# Revit family: LED-PL-CSVT
name_source: partatom
category: Осветительные приборы
units: mm (PartAtom-declared; Revit-internal decimal feet)

## family parameters
Всегда вертикально = Нет
Источник света = Да
На основе рабочей плоскости = Нет
Общий = Нет
При загрузке вырезать с полостями = Нет
Размер круглого соединителя = Использовать диаметр
Тип детали = Нормальный
Точка расчета площади = Да

## types (9) — shared parameters
ADSK_Единица измерения = шт.
ADSK_Завод-изготовитель = ЗАО «Центрстройсвет»
ADSK_Классификация нагрузок = Прочее
ADSK_Количество фаз = 1
ADSK_Количество фаз числовое = 1
ADSK_Коэффициент мощности = 0.92
ADSK_Напряжение = 230 В
ADSK_Ток = 0 А
URL = http://csvt.ru
Видимая форма излучения при визуализации = Да
Высота = 10 мм
Изготовитель = ЗАО «Центрстройсвет»
Материал светильника = RAL 9001
Материал стекла = RAL светящийся
Светофильтр = 16777215
Смещение цветовой температуры при затухании лампы = <Нет>
Угол наклона = 90.00°

## per-type parameters (varying)
| type | ADSK_Код изделия | ADSK_Масса | ADSK_Наименование | ADSK_Номинальная мощность | ADSK_Обозначение | ADSK_Полная мощность | L | L1 | Длина | Излучение по длине прямоугольника | Излучение по ширине прямоугольника | Файл фотометрической сетки | Ширина |
| LED PL-CSVT-36 595x595х10 (KROKUS) (IP54/IP20, 4000K, белый) | ЦБ000007456 | 3.2 | Ультратонкая светодиодная панель LED PL-CSVT-36 595x595х10 (KROKUS) (IP54/IP20, 4000K, белый) | 36 Вт | LED PL-CSVT-36 595x595х10 (KROKUS) (IP54/IP20, 4000K, белый) | 39 В·А | 298 мм | 298 мм | 595 мм | 555 мм | 555 мм | Светильник LED-PL-CSVT-36-(595х595).IES | 595 мм |
| LED PL-CSVT-36 595x595 х10 (KROKUS) (IP54/IP20, 4000K, белый) c БАП на 1 час | ЦБ000007518 | 3.2 | Ультратонкая светодиодная панель LED PL-CSVT-36 595x595 х10 (KROKUS) (IP54/IP20, 4000K, белый) c БАП на 1 час | 36 Вт | LED PL-CSVT-36 595x595 х10 (KROKUS) (IP54/IP20, 4000K, белый) | 39 В·А | 298 мм | 298 мм | 595 мм | 555 мм | 555 мм | Светильник LED-PL-CSVT-36-(595х595).IES | 595 мм |
| LED PL-CSVT-36 595x595 х10 (KROKUS) (IP54/IP20, 4000K, белый) c БАП на 3 часа | ЦБ000007519 | 3.2 | Ультратонкая светодиодная панель LED PL-CSVT-36 595x595 х10 (KROKUS) (IP54/IP20, 4000K, белый) c БАП на 3 часа | 36 Вт | LED PL-CSVT-36 595x595 х10 (KROKUS) (IP54/IP20, 4000K, белый) | 39 В·А | 298 мм | 298 мм | 595 мм | 555 мм | 555 мм | Светильник LED-PL-CSVT-36-(595х595).IES | 595 мм |
| LED PL-CSVT-18 295x595 х10 (KROKUS) (IP54/IP20, 4000K, белый) | ЦБ000007513 | 1.8 | Ультратонкая светодиодная панель LED PL-CSVT-18 295x595 х10 (KROKUS) (IP54/IP20, 4000K, белый) | 18 Вт | LED PL-CSVT-18 295x595 х10 (KROKUS) (IP54/IP20, 4000K, белый) | 20 В·А | 298 мм | 148 мм | 595 мм | 555 мм | 255 мм | Светильник LED-PL-CSVT-18-(295х595).IES | 295 мм |
| LED PL-CSVT-38 295x1195 х10 (KROKUS) (IP54/IP20, 4000K, белый) | ЦБ000007521 | 3.4 | Ультратонкая светодиодная панель LED PL-CSVT-38 295x1195 х10 (KROKUS) (IP54/IP20, 4000K, белый) | 38 Вт | LED PL-CSVT-38 295x1195 х10 (KROKUS) (IP54/IP20, 4000K, белый) | 41 В·А | 598 мм | 148 мм | 1195 мм | 1155 мм | 255 мм | Светильник LED-PL-CSVT-38-(295x1195).IES | 295 мм |
| LED PL-CSVT-38 295x1195 х10 (KROKUS) (IP54/IP20, 4000K, белый) c БАП на 1 час | ЦБ000007522 | 3.4 | Ультратонкая светодиодная панель LED PL-CSVT-38 295x1195 х10 (KROKUS) (IP54/IP20, 4000K, белый) c БАП на 1 час | 38 Вт | LED PL-CSVT-38 295x1195 х10 (KROKUS) (IP54/IP20, 4000K, белый) | 41 В·А | 598 мм | 148 мм | 1195 мм | 1155 мм | 255 мм | Светильник LED-PL-CSVT-38-(295x1195).IES | 295 мм |
| LED PL-CSVT-38 295x1195 х10 (KROKUS) (IP54/IP20, 4000K, белый) c БАП на 3 часа | ЦБ000007523 | 3.4 | Ультратонкая светодиодная панель LED PL-CSVT-38 295x1195 х10 (KROKUS) (IP54/IP20, 4000K, белый) c БАП на 3 часа | 38 Вт | LED PL-CSVT-38 295x1195 х10 (KROKUS) (IP54/IP20, 4000K, белый) | 41 В·А | 598 мм | 148 мм | 1195 мм | 1155 мм | 255 мм | Светильник LED-PL-CSVT-38-(295x1195).IES | 295 мм |
| LED PL-CSVT-36 588х588 х10 (KROKUS) (IP54/IP20, 4000К, белый, грильято) | ЦБ000010147 | 3.4 | Ультратонкая светодиодная панель LED PL-CSVT-36 588х588 х10 (KROKUS) (IP54/IP20, 4000К, белый, грильято) | 38 Вт | LED PL-CSVT-36 588х588 х10 (KROKUS) (IP54/IP20, 4000К, белый, грильято) | 41 В·А | 294 мм | 294 мм | 588 мм | 548 мм | 548 мм | Светильник LED-PL-CSVT-36-(595х595).IES | 588 мм |
| LED PL-CSVT-36 588х588 х10 (KROKUS) (IP54/IP20, 5000К, белый, грильято) | ЦБ000009945 | 3.4 | Ультратонкая светодиодная панель LED PL-CSVT-36 588х588 х10 (KROKUS) (IP54/IP20, 5000К, белый, грильято) | 38 Вт | LED PL-CSVT-36 588х588 х10 (KROKUS) (IP54/IP20, 5000К, белый, грильято) | 41 В·А | 294 мм | 294 мм | 588 мм | 548 мм | 548 мм | Светильник LED-PL-CSVT-36-(595х595).IES | 588 мм |
